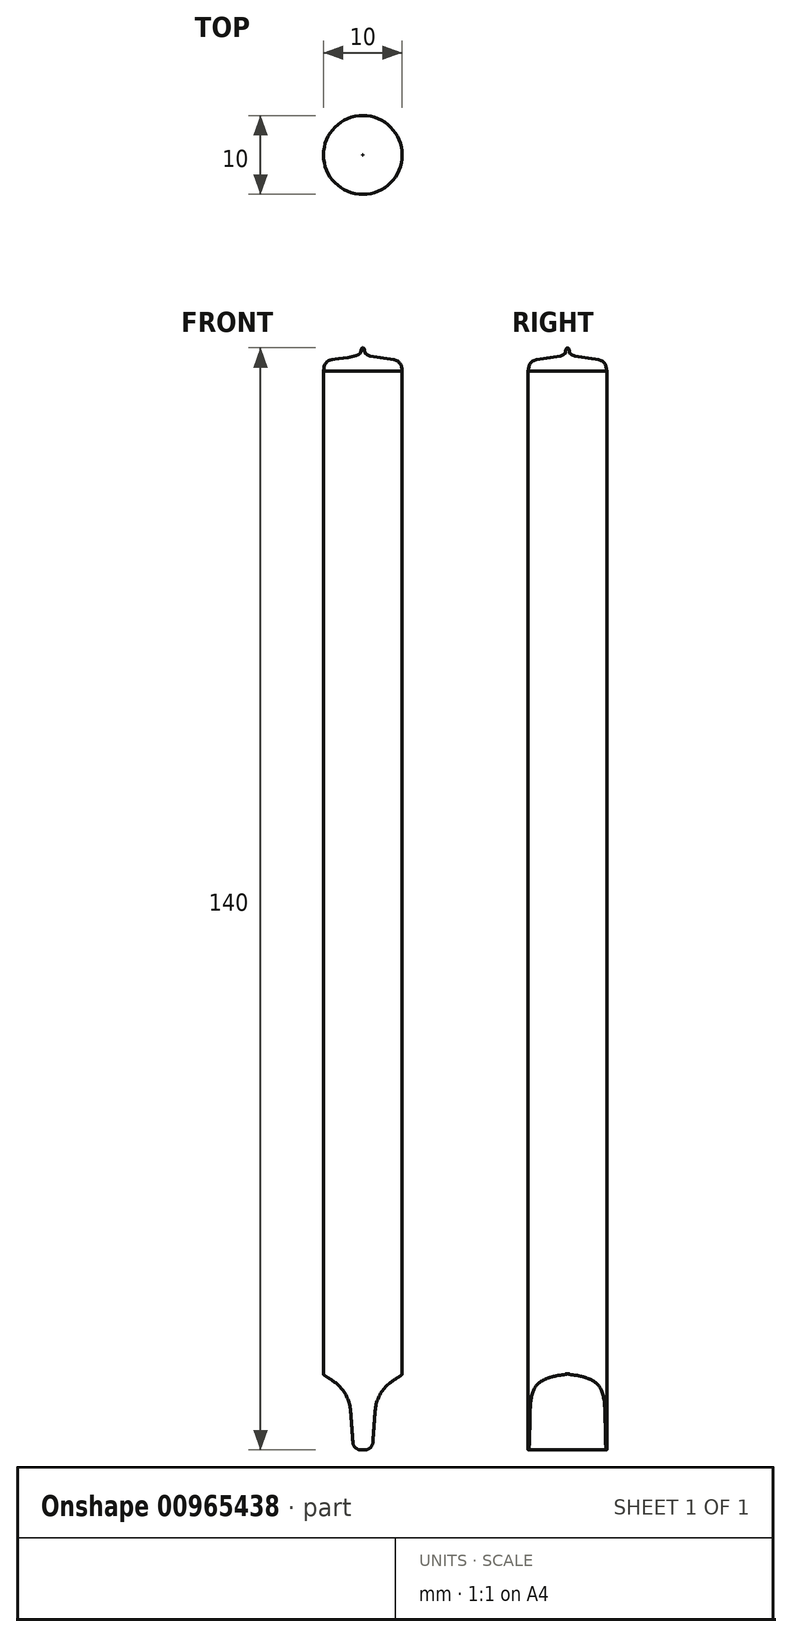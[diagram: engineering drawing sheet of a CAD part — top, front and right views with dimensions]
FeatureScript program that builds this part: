
annotation { "Feature Type Name" : "Feature", "Feature Type Description" : "" }
export const myFeature = defineFeature(function(context is Context, id is Id, definition is map)
    precondition{}
    {
        {
            var Q0;
            Q0=qCreatedBy(makeId("Top.planeOp"),FACE);
            var sketch = newSketch(context, id + "F0", { "sketchPlane" : qUnion([Q0])});
            skCircle(sketch, "E0", {"center": v(0, 0) * mm, "radius": 5 * mm});
            skSolve(sketch);
        }
        {
            var Q0;
            Q0 = qSketchRegion(id + "F0", true);
            extrude(context, id + "F1", {"entities" : qUnion([Q0]), "depth" : 140 * mm, "offsetDistance" : 25 * mm});
        }
        {
            var Q0;
            Q0=qCreatedBy(makeId("Front.planeOp"),FACE);
            var sketch = newSketch(context, id + "F2", { "sketchPlane" : qUnion([Q0])});
            skLineSegment(sketch, "E1", {"start": v(-4.86, 9.77) * mm, "end": v(4.86, 9.77) * mm});
            skLineSegment(sketch, "E2", {"start": v(4.93, 9.5) * mm, "end": v(3.84, 8.8) * mm});
            skLineSegment(sketch, "E3", {"start": v(1.56, 4.95) * mm, "end": v(1.27, 0.93) * mm});
            skLineSegment(sketch, "E4", {"start": v(0.27, 0) * mm, "end": v(0, 0) * mm});
            skLineSegment(sketch, "E5", {"start": v(0, 0) * mm, "end": v(-0.27, 0) * mm});
            skLineSegment(sketch, "E6", {"start": v(-1.27, 0.93) * mm, "end": v(-1.56, 4.95) * mm});
            skLineSegment(sketch, "E7", {"start": v(-3.84, 8.8) * mm, "end": v(-4.93, 9.5) * mm});
            skLineSegment(sketch, "E8", {"start": v(0, 0) * mm, "end": v(0, 10.49) * mm, "construction": true});
            skPoint(sketch, "E9", {"position": v(3.54, 8.6) * mm});
            skPoint(sketch, "E10", {"position": v(-3.54, 8.6) * mm});
            skPoint(sketch, "E11.visualSharp", {"position": v(1.74, 7.44) * mm});
            skArc(sketch, "E11.filletArc", {"start": v(3.84, 8.8) * mm, "mid": v(2.24, 7.14) * mm, "end": v(1.56, 4.95) * mm});
            skPoint(sketch, "E12.visualSharp", {"position": v(-1.74, 7.44) * mm});
            skArc(sketch, "E12.filletArc", {"start": v(-1.56, 4.95) * mm, "mid": v(-2.24, 7.14) * mm, "end": v(-3.84, 8.8) * mm});
            skPoint(sketch, "E13.visualSharp", {"position": v(-1.2, 0) * mm});
            skArc(sketch, "E13.filletArc", {"start": v(-1.27, 0.93) * mm, "mid": v(-0.95, 0.27) * mm, "end": v(-0.27, 0) * mm});
            skPoint(sketch, "E14.visualSharp", {"position": v(1.2, 0) * mm});
            skArc(sketch, "E14.filletArc", {"start": v(0.27, 0) * mm, "mid": v(0.95, 0.27) * mm, "end": v(1.27, 0.93) * mm});
            skPoint(sketch, "E15.visualSharp", {"position": v(-5.34, 9.77) * mm});
            skArc(sketch, "E15.filletArc", {"start": v(-4.86, 9.77) * mm, "mid": v(-5, 9.66) * mm, "end": v(-4.93, 9.5) * mm});
            skPoint(sketch, "E16.visualSharp", {"position": v(5.34, 9.77) * mm});
            skArc(sketch, "E16.filletArc", {"start": v(4.93, 9.5) * mm, "mid": v(5, 9.66) * mm, "end": v(4.86, 9.77) * mm});
            skLineSegment(sketch, "E17", {"start": v(5, 0) * mm, "end": v(-5, 0) * mm});
            skLineSegment(sketch, "E18", {"start": v(5, 9.66) * mm, "end": v(5.14, 9.33) * mm});
            skLineSegment(sketch, "E19", {"start": v(5.14, 9.33) * mm, "end": v(6.05, 5.58) * mm});
            skLineSegment(sketch, "E20", {"start": v(6.05, 5.58) * mm, "end": v(8.48, -1.74) * mm});
            skLineSegment(sketch, "E21", {"start": v(8.48, -1.74) * mm, "end": v(0, -1.74) * mm});
            skLineSegment(sketch, "E22", {"start": v(0, -1.74) * mm, "end": v(-9.13, -1.74) * mm});
            skLineSegment(sketch, "E23", {"start": v(-9.13, -1.74) * mm, "end": v(-10.44, 4.6) * mm});
            skLineSegment(sketch, "E24", {"start": v(-10.44, 4.6) * mm, "end": v(-7.44, 9.33) * mm});
            skLineSegment(sketch, "E25", {"start": v(-7.44, 9.33) * mm, "end": v(-5.64, 8.8) * mm});
            skLineSegment(sketch, "E26", {"start": v(-5.64, 8.8) * mm, "end": v(-5, 9.66) * mm});
            skSolve(sketch);
        }
        {
            var Q0;
            {var subQ1=sQuery(id+"F2.wireOp",EDGE,"E2");Q0=makeQuery(id+"F2.imprint","IMPRINT",FACE,{"disambiguationData":[TD([[makeQuery(id+"F2.imprint","IMPRINT",EDGE,{"derivedFrom":subQ1}),1.0]])]});}
            extrude(context, id + "F3", {"entities" : qUnion([Q0]), "operationType" : NewBodyOperationType.REMOVE, "endBound" : BoundingType.SYMMETRIC, "oppositeDirection" : true, "depth" : 23.1 * mm, "offsetDistance" : 25 * mm});
        }
        {
            var Q0;
            Q0=qCreatedBy(makeId("Right.planeOp"),FACE);
            var sketch = newSketch(context, id + "F4", { "sketchPlane" : qUnion([Q0])});
            skLineSegment(sketch, "E27", {"start": v(0, 141.23) * mm, "end": v(0, 137.34) * mm, "construction": true});
            skLineSegment(sketch, "E28.bottom", {"start": v(-5.05, 140.2) * mm, "end": v(0, 140.2) * mm});
            skLineSegment(sketch, "E28.top", {"start": v(-5.05, 136.64) * mm, "end": v(0, 136.64) * mm});
            skLineSegment(sketch, "E28.left", {"start": v(-5.05, 140.2) * mm, "end": v(-5.05, 136.64) * mm});
            skLineSegment(sketch, "E28.right", {"start": v(0, 140.2) * mm, "end": v(0, 136.64) * mm});
            skFitSpline(sketch, "E29", {"points": [v(0, 140) * mm, v(-0.17, 139.93) * mm, v(-0.22, 139.74) * mm, v(-0.27, 139.43) * mm, v(-0.5, 139.12) * mm, v(-3.52, 138.56) * mm, v(-4.4, 138.34) * mm, v(-4.76, 138) * mm, v(-4.88, 137.75) * mm, v(-5.05, 136.64) * mm], "startDerivative": vector(-3.14, -0.91) * mm, "endDerivative": vector(-1.04, -8.77) * mm});
            skSolve(sketch);
        }
        {
            var Q0;
            {var subQ0=sQuery(id+"F4.wireOp",EDGE,"E28.bottom");Q0=makeQuery(id+"F4.imprint","IMPRINT",FACE,{"disambiguationData":[TD([[makeQuery(id+"F4.imprint","IMPRINT",EDGE,{"derivedFrom":subQ0}),-1.0]])]});}
            var Q1;
            Q1=sQuery(id+"F4.wireOp",EDGE,"E27");
            revolve(context, id + "F5", {"operationType" : NewBodyOperationType.REMOVE, "surfaceOperationType" : NewSurfaceOperationType.NEW, "entities" : qUnion([Q0]), "axis" : qUnion([Q1]), "revolveType" : RevolveType.FULL, "oppositeDirection" : true});
        }
    });
